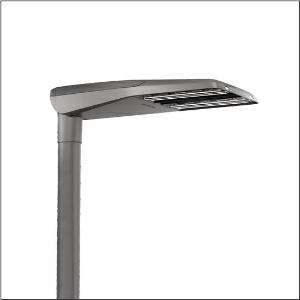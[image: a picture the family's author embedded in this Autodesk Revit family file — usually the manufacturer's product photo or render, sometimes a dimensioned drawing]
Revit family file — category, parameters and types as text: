
# Revit family: streetlight_sl_11_iq_midi___st1_2a_5xc3a41e08le_4284
name_source: partatom
category: Lighting Fixtures
units: mm (PartAtom-declared; Revit-internal decimal feet)

## family parameters
Cut with Voids When Loaded = No
Host = Face
Light Source = No
Part Type = Normal
Room Calculation Point = No
Round Connector Dimension = Use Diameter
Shared = No

## types (1)
- --- (1 x LED, 9590 lm, 60.4 W, 4000K)
    Apparent Load = 60 VA
    CIE Flux Codes = 32 70 96 100 100
    Color Rendering = 70
    Color Temperature = 4000K
    Default Elevation = 1800 mm
    Description = Streetlight SL 11 iQ midi, mast luminaire, primary light control with 3 zone facetted reflector, of plastic, silver coated, highly specular, primary optical cover: cover, of PMMA, transparent, light distribution: ST1.2a, light emission: direct distribution, primary light characteristic: asymmetric, installation type: post-top, side-entry, LED, High Power LED, rated luminous flux: 9.590lm, luminous efficacy: 159lm/W, light colour: 740, colour temperature: 4000K, control: optimised constant luminous flux control (CLO 2.0), Desk-Remote (wireless, voltage-free reading and setting of iQ features in the workshop via application-optimized NFC function/RFID function), Light-Fading, Smart-Wire, Night-Set, Lumen-Switch, Temp-Guard, Auto-Match, with cable H07RN-F 5x 1.5mm², mains connection: 230..240V, AC, 50/60Hz, connection cable pre-assembled, cable length: 8,5m, start of lifetime: 60W, end of service life: 63W, reduction: 30W, luminaire housing, of diecast aluminium, powder-coated, Siteco® metallic grey (DB 702S), please order mast flange separately, inclination adjustable without tools: 0°, 5°, 10°, 15° (post-top) | 0°, -5°, -10°, -15° (side-entry), sealing non-destructively replaceable, multi-level sealing system, length: 780mm, width: 376mm, height: 118mm, mast flange for spigot size: 42mm (side-entry): 5XC10008XM4, 60/48mm (side-entry/post-top): 5XC10108XM2, 76/60mm (side-entry/post-top): 5XC10108XM1, equipment: standard, protection rating (complete): IP66, insulation class (complete): insulation class II (safety insulation), certification: CE, ENEC, VDE, impact resistance: IK09, permissible operating ambient temperature for outdoor applications: -25..+50°C, standard-compliant lighting for roads and squares, Environmental Product Declaration (EPD) tested and certified by an independent institute, packaging unit: 1 piece

Light Distribution: ST1.2a
    Height = 118 mm
    Lamp = 1 x LED
    Lamp Light Flux = 9590 lm
    Lamp Power = 60.4 W
    Lamp count = 1
    Length = 780 mm
    Luminous efficacy = 159 lm/W
    Manufacturer = Siteco
    ModVariant = No
    Model = 5XC3A41E08LE
    Number of Poles = 1
    OnlyDefault = Yes
    Power Factor = 1
    Product Name = Streetlight SL 11 iQ midi | ST1.2a
    Product group = mast luminaire | pylon top
    ProductGroupID = 6100
    Protection Class = Protection class II
    Protection Degree = IP 66
    RLX_Detail_Level = 1
    RLX_Emergency_Light_Flux = 0 lm
    RLX_Emergency_Type = 0
    RLX_Emergency_Type_DB = No
    RlxData = <blob elided: 70725 chars, md5=5cc22504>
    Socket = socket
    Standby Power = 0 W
    System Light Flux = 9590 lm
    System Power = 60 W
    Type Comments = factory setting: luminous flux: 100 % | dim-lin: 254 | 520 mA
    Type Image = l_1005960.jpg
    URL = http://relux.com
    VarID = @adj_150829
    Voltage = 0 V
    Weight = 0.00 kg
    Width = 376 mm

## geometry (parser evidence)
native form markers: Blend x4, Sweep x8
no freeform markers — native parametric forms only
